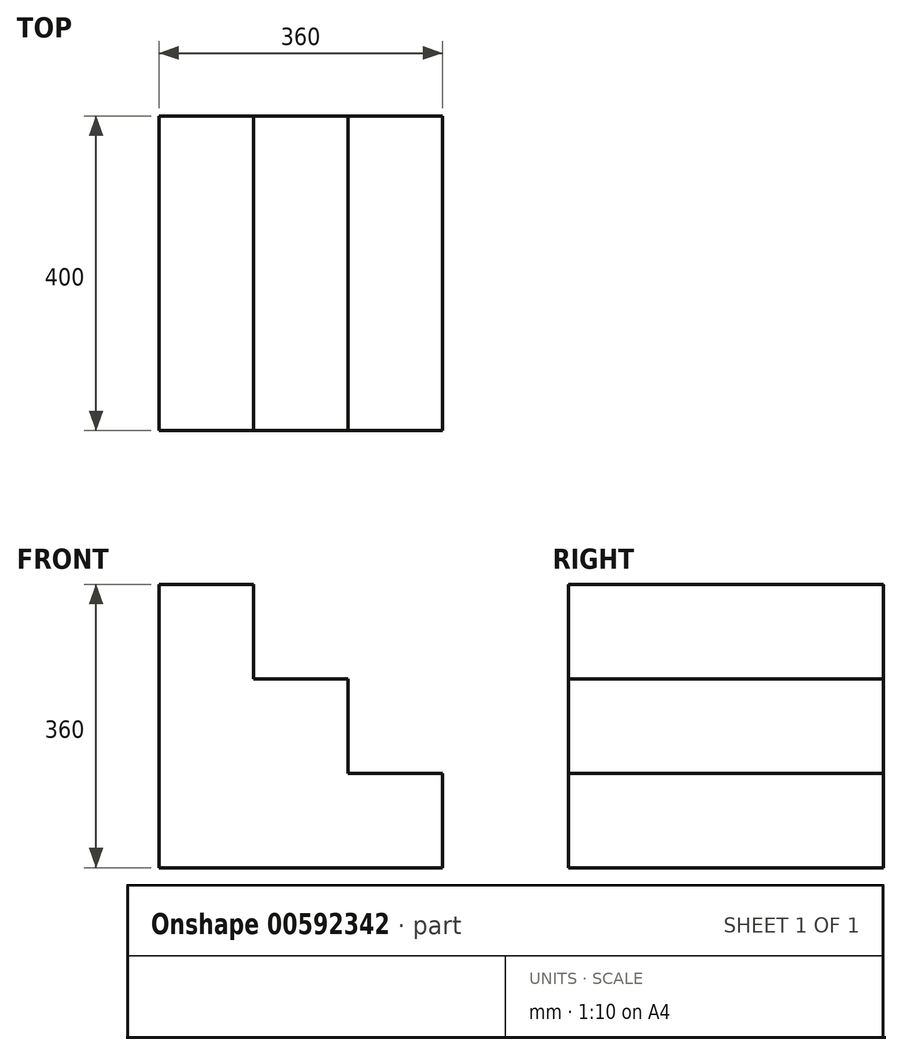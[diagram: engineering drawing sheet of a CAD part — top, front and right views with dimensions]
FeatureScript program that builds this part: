
annotation { "Feature Type Name" : "Feature", "Feature Type Description" : "" }
export const myFeature = defineFeature(function(context is Context, id is Id, definition is map)
    precondition{}
    {
        {
            var Q0;
            Q0=qCreatedBy(makeId("Front.planeOp"),FACE);
            var sketch = newSketch(context, id + "F0", { "sketchPlane" : qUnion([Q0])});
            skLineSegment(sketch, "E0", {"start": v(0, 0) * mm, "end": v(360, 0) * mm});
            skLineSegment(sketch, "E1", {"start": v(360, 0) * mm, "end": v(360, 120) * mm});
            skLineSegment(sketch, "E2", {"start": v(360, 120) * mm, "end": v(240, 120) * mm});
            skLineSegment(sketch, "E3", {"start": v(240, 240) * mm, "end": v(240, 120) * mm});
            skLineSegment(sketch, "E4", {"start": v(240, 240) * mm, "end": v(120, 240) * mm});
            skLineSegment(sketch, "E5", {"start": v(120, 360) * mm, "end": v(120, 240) * mm});
            skLineSegment(sketch, "E6", {"start": v(0, 0) * mm, "end": v(0, 360) * mm});
            skLineSegment(sketch, "E7", {"start": v(0, 360) * mm, "end": v(120, 360) * mm});
            skSolve(sketch);
        }
        {
            var Q0;
            Q0=makeQuery(id+"F0.imprint","IMPRINT",FACE,{"disambiguationData":[TD([[makeQuery(id+"F0.imprint","IMPRINT",EDGE,{"derivedFrom":sQuery(id+"F0.wireOp",EDGE,"E0")}),1.0]])]});
            extrude(context, id + "F1", {"entities" : qUnion([Q0]), "depth" : 400 * mm, "offsetDistance" : 25 * mm});
        }
    });
